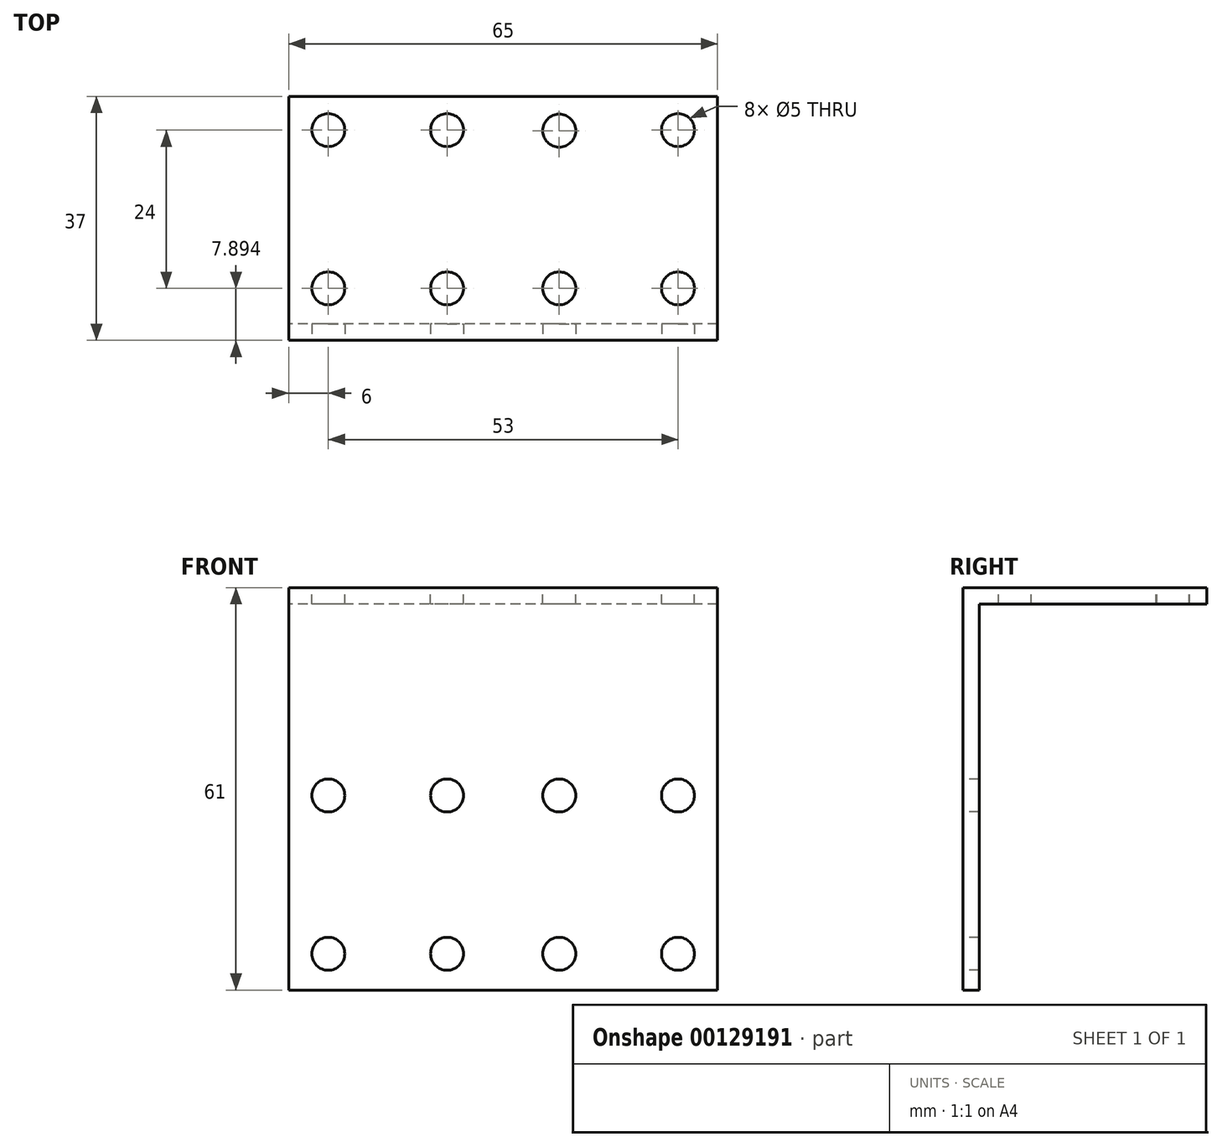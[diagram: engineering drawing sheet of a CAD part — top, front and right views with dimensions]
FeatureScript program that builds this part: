
annotation { "Feature Type Name" : "Feature", "Feature Type Description" : "" }
export const myFeature = defineFeature(function(context is Context, id is Id, definition is map)
    precondition{}
    {
        {
            var Q0;
            Q0=qCreatedBy(makeId("Right.planeOp"),FACE);
            var sketch = newSketch(context, id + "F0", { "sketchPlane" : qUnion([Q0])});
            skLineSegment(sketch, "E0.bottom", {"start": v(0, 0) * mm, "end": v(2.5, 0) * mm});
            skLineSegment(sketch, "E0.top", {"start": v(0, -58.5) * mm, "end": v(2.5, -58.5) * mm});
            skLineSegment(sketch, "E0.left", {"start": v(0, 0) * mm, "end": v(0, -58.5) * mm});
            skLineSegment(sketch, "E0.right", {"start": v(2.5, 0) * mm, "end": v(2.5, -58.5) * mm});
            skLineSegment(sketch, "E1.bottom", {"start": v(0, 0) * mm, "end": v(37, 0) * mm});
            skLineSegment(sketch, "E1.top", {"start": v(0, 2.5) * mm, "end": v(37, 2.5) * mm});
            skLineSegment(sketch, "E1.left", {"start": v(0, 0) * mm, "end": v(0, 2.5) * mm});
            skLineSegment(sketch, "E1.right", {"start": v(37, 0) * mm, "end": v(37, 2.5) * mm});
            skSolve(sketch);
        }
        {
            var Q0;
            Q0=makeQuery(id+"F0.imprint","IMPRINT",FACE,{"disambiguationData":[TD([[makeQuery(id+"F0.imprint","IMPRINT",EDGE,{"derivedFrom":sQuery(id+"F0.wireOp",EDGE,"E1.top")}),-1.0]])]});
            var Q1;
            Q1=makeQuery(id+"F0.imprint","IMPRINT",FACE,{"disambiguationData":[TD([[makeQuery(id+"F0.imprint","IMPRINT",EDGE,{"derivedFrom":sQuery(id+"F0.wireOp",EDGE,"E0.top")}),1.0]])]});
            extrude(context, id + "F1", {"entities" : qUnion([Q0, Q1]), "endBound" : BoundingType.SYMMETRIC, "depth" : 65 * mm});
        }
        {
            var Q0;
            Q0=qCreatedBy(makeId("Front.planeOp"),FACE);
            var sketch = newSketch(context, id + "F2", { "sketchPlane" : qUnion([Q0])});
            skLineSegment(sketch, "E2.bottom", {"start": v(-32.5, 2.5) * mm, "end": v(32.5, 2.5) * mm, "construction": true});
            skLineSegment(sketch, "E2.left", {"start": v(-32.5, 2.5) * mm, "end": v(-32.5, -32.5) * mm, "construction": true});
            skLineSegment(sketch, "E3", {"start": v(-34.69, -29) * mm, "end": v(41.82, -29) * mm, "construction": true});
            skCircle(sketch, "E4", {"center": v(-26.5, -29) * mm, "radius": 2.5 * mm});
            skCircle(sketch, "E5", {"center": v(-8.5, -29) * mm, "radius": 2.5 * mm});
            skCircle(sketch, "E6", {"center": v(8.5, -29) * mm, "radius": 2.5 * mm});
            skCircle(sketch, "E7", {"center": v(26.5, -29) * mm, "radius": 2.5 * mm});
            skLineSegment(sketch, "E8", {"start": v(-40, -53) * mm, "end": v(46.08, -53) * mm, "construction": true});
            skCircle(sketch, "E9", {"center": v(-26.5, -53) * mm, "radius": 2.5 * mm});
            skCircle(sketch, "E10", {"center": v(-8.5, -53) * mm, "radius": 2.5 * mm});
            skCircle(sketch, "E11", {"center": v(8.5, -53) * mm, "radius": 2.5 * mm});
            skCircle(sketch, "E12", {"center": v(26.5, -53) * mm, "radius": 2.5 * mm});
            skLineSegment(sketch, "E13", {"start": v(8.5, -15.9) * mm, "end": v(8.5, -70.5) * mm});
            skLineSegment(sketch, "E14", {"start": v(26.5, -15.26) * mm, "end": v(26.5, -64.56) * mm});
            skLineSegment(sketch, "E15", {"start": v(-8.5, -14.62) * mm, "end": v(-8.5, -68.69) * mm});
            skLineSegment(sketch, "E16", {"start": v(-26.5, -12.16) * mm, "end": v(-26.5, -65.46) * mm});
            skSolve(sketch);
        }
        {
            var Q0;
            Q0=makeQuery(id+"F2.imprint","IMPRINT",FACE,{"disambiguationData":[TD([[makeQuery(id+"F2.imprint","IMPRINT",EDGE,{"derivedFrom":sQuery(id+"F2.wireOp",EDGE,"E4")}),1.0]])]});
            var Q1;
            Q1=makeQuery(id+"F2.imprint","IMPRINT",FACE,{"disambiguationData":[TD([[makeQuery(id+"F2.imprint","IMPRINT",EDGE,{"derivedFrom":sQuery(id+"F2.wireOp",EDGE,"E5")}),1.0]])]});
            var Q2;
            Q2=makeQuery(id+"F2.imprint","IMPRINT",FACE,{"disambiguationData":[TD([[makeQuery(id+"F2.imprint","IMPRINT",EDGE,{"derivedFrom":sQuery(id+"F2.wireOp",EDGE,"E6")}),1.0]])]});
            var Q3;
            Q3=makeQuery(id+"F2.imprint","IMPRINT",FACE,{"disambiguationData":[TD([[makeQuery(id+"F2.imprint","IMPRINT",EDGE,{"derivedFrom":sQuery(id+"F2.wireOp",EDGE,"E7")}),1.0]])]});
            var Q4;
            Q4=makeQuery(id+"F2.imprint","IMPRINT",FACE,{"disambiguationData":[TD([[makeQuery(id+"F2.imprint","IMPRINT",EDGE,{"derivedFrom":sQuery(id+"F2.wireOp",EDGE,"E9")}),1.0]])]});
            var Q5;
            {var subQ0=sQuery(id+"F2.wireOp",EDGE,"E15");var subQ1=sQuery(id+"F2.wireOp",EDGE,"E10");var subQ2=makeQuery(id+"F2.imprint","INTERSECT",VERTEX,{"disambiguationData":[OD(0.0)],"derivedFrom":[subQ1,subQ0]});Q5=makeQuery(id+"F2.imprint","IMPRINT",FACE,{"disambiguationData":[TD([[makeQuery(id+"F2.imprint","IMPRINT",EDGE,{"disambiguationData":[TD([[subQ2,1.0]])],"derivedFrom":subQ1}),1.0]])]});}
            var Q6;
            {var subQ0=sQuery(id+"F2.wireOp",EDGE,"E15");var subQ1=sQuery(id+"F2.wireOp",EDGE,"E10");var subQ2=makeQuery(id+"F2.imprint","INTERSECT",VERTEX,{"disambiguationData":[OD(0.0)],"derivedFrom":[subQ1,subQ0]});Q6=makeQuery(id+"F2.imprint","IMPRINT",FACE,{"disambiguationData":[TD([[makeQuery(id+"F2.imprint","IMPRINT",EDGE,{"disambiguationData":[TD([[subQ2,-1.0]])],"derivedFrom":subQ1}),1.0]])]});}
            var Q7;
            {var subQ0=sQuery(id+"F2.wireOp",EDGE,"E13");var subQ1=sQuery(id+"F2.wireOp",EDGE,"E11");var subQ2=makeQuery(id+"F2.imprint","INTERSECT",VERTEX,{"disambiguationData":[OD(0.0)],"derivedFrom":[subQ1,subQ0]});Q7=makeQuery(id+"F2.imprint","IMPRINT",FACE,{"disambiguationData":[TD([[makeQuery(id+"F2.imprint","IMPRINT",EDGE,{"disambiguationData":[TD([[subQ2,1.0]])],"derivedFrom":subQ1}),1.0]])]});}
            var Q8;
            {var subQ0=sQuery(id+"F2.wireOp",EDGE,"E13");var subQ1=sQuery(id+"F2.wireOp",EDGE,"E11");var subQ2=makeQuery(id+"F2.imprint","INTERSECT",VERTEX,{"disambiguationData":[OD(0.0)],"derivedFrom":[subQ1,subQ0]});Q8=makeQuery(id+"F2.imprint","IMPRINT",FACE,{"disambiguationData":[TD([[makeQuery(id+"F2.imprint","IMPRINT",EDGE,{"disambiguationData":[TD([[subQ2,-1.0]])],"derivedFrom":subQ1}),1.0]])]});}
            var Q9;
            {var subQ0=sQuery(id+"F2.wireOp",EDGE,"E14");var subQ1=sQuery(id+"F2.wireOp",EDGE,"E12");var subQ2=makeQuery(id+"F2.imprint","INTERSECT",VERTEX,{"disambiguationData":[OD(0.0)],"derivedFrom":[subQ1,subQ0]});Q9=makeQuery(id+"F2.imprint","IMPRINT",FACE,{"disambiguationData":[TD([[makeQuery(id+"F2.imprint","IMPRINT",EDGE,{"disambiguationData":[TD([[subQ2,1.0]])],"derivedFrom":subQ1}),1.0]])]});}
            var Q10;
            {var subQ0=sQuery(id+"F2.wireOp",EDGE,"E14");var subQ1=sQuery(id+"F2.wireOp",EDGE,"E12");var subQ2=makeQuery(id+"F2.imprint","INTERSECT",VERTEX,{"disambiguationData":[OD(0.0)],"derivedFrom":[subQ1,subQ0]});Q10=makeQuery(id+"F2.imprint","IMPRINT",FACE,{"disambiguationData":[TD([[makeQuery(id+"F2.imprint","IMPRINT",EDGE,{"disambiguationData":[TD([[subQ2,-1.0]])],"derivedFrom":subQ1}),1.0]])]});}
            extrude(context, id + "F3", {"entities" : qUnion([Q0, Q1, Q2, Q3, Q4, Q5, Q6, Q7, Q8, Q9, Q10]), "operationType" : NewBodyOperationType.REMOVE, "endBound" : BoundingType.SYMMETRIC, "oppositeDirection" : true, "depth" : 10 * mm});
        }
        {
            var Q0;
            Q0=makeQuery(id+"F1.opExtrude","SWEPT_FACE",FACE,{"disambiguationData":[OSD([sQuery(id+"F0.wireOp",EDGE,"E1.top")])]});
            var sketch = newSketch(context, id + "F4", { "sketchPlane" : qUnion([Q0])});
            skLineSegment(sketch, "E17", {"start": v(-26.5, 45.64) * mm, "end": v(-26.5, -8.44) * mm, "construction": true});
            skLineSegment(sketch, "E18", {"start": v(-42.57, 7.9) * mm, "end": v(45.18, 7.9) * mm, "construction": true});
            skCircle(sketch, "E19", {"center": v(-26.5, 7.9) * mm, "radius": 2.5 * mm});
            skCircle(sketch, "E20", {"center": v(-8.5, 7.9) * mm, "radius": 2.5 * mm});
            skCircle(sketch, "E21", {"center": v(8.5, 7.9) * mm, "radius": 2.5 * mm});
            skCircle(sketch, "E22", {"center": v(26.5, 7.9) * mm, "radius": 2.5 * mm});
            skLineSegment(sketch, "E23", {"start": v(-43.35, 31.9) * mm, "end": v(45.05, 31.9) * mm, "construction": true});
            skCircle(sketch, "E24", {"center": v(-26.5, 31.9) * mm, "radius": 2.5 * mm});
            skCircle(sketch, "E25", {"center": v(-8.5, 31.9) * mm, "radius": 2.5 * mm});
            skCircle(sketch, "E26", {"center": v(8.5, 31.8) * mm, "radius": 2.5 * mm});
            skCircle(sketch, "E27", {"center": v(26.5, 31.9) * mm, "radius": 2.5 * mm});
            skSolve(sketch);
        }
        {
            var Q0;
            Q0=makeQuery(id+"F4.imprint","IMPRINT",FACE,{"disambiguationData":[TD([[makeQuery(id+"F4.imprint","IMPRINT",EDGE,{"derivedFrom":sQuery(id+"F4.wireOp",EDGE,"E19")}),1.0]])]});
            var Q1;
            Q1=makeQuery(id+"F4.imprint","IMPRINT",FACE,{"disambiguationData":[TD([[makeQuery(id+"F4.imprint","IMPRINT",EDGE,{"derivedFrom":sQuery(id+"F4.wireOp",EDGE,"E24")}),1.0]])]});
            var Q2;
            Q2=makeQuery(id+"F4.imprint","IMPRINT",FACE,{"disambiguationData":[TD([[makeQuery(id+"F4.imprint","IMPRINT",EDGE,{"derivedFrom":sQuery(id+"F4.wireOp",EDGE,"E25")}),1.0]])]});
            var Q3;
            Q3=makeQuery(id+"F4.imprint","IMPRINT",FACE,{"disambiguationData":[TD([[makeQuery(id+"F4.imprint","IMPRINT",EDGE,{"derivedFrom":sQuery(id+"F4.wireOp",EDGE,"E20")}),1.0]])]});
            var Q4;
            Q4=makeQuery(id+"F4.imprint","IMPRINT",FACE,{"disambiguationData":[TD([[makeQuery(id+"F4.imprint","IMPRINT",EDGE,{"derivedFrom":sQuery(id+"F4.wireOp",EDGE,"E21")}),1.0]])]});
            var Q5;
            Q5=makeQuery(id+"F4.imprint","IMPRINT",FACE,{"disambiguationData":[TD([[makeQuery(id+"F4.imprint","IMPRINT",EDGE,{"derivedFrom":sQuery(id+"F4.wireOp",EDGE,"E26")}),1.0]])]});
            var Q6;
            Q6=makeQuery(id+"F4.imprint","IMPRINT",FACE,{"disambiguationData":[TD([[makeQuery(id+"F4.imprint","IMPRINT",EDGE,{"derivedFrom":sQuery(id+"F4.wireOp",EDGE,"E27")}),1.0]])]});
            var Q7;
            Q7=makeQuery(id+"F4.imprint","IMPRINT",FACE,{"disambiguationData":[TD([[makeQuery(id+"F4.imprint","IMPRINT",EDGE,{"derivedFrom":sQuery(id+"F4.wireOp",EDGE,"E22")}),1.0]])]});
            extrude(context, id + "F5", {"entities" : qUnion([Q0, Q1, Q2, Q3, Q4, Q5, Q6, Q7]), "operationType" : NewBodyOperationType.REMOVE, "endBound" : BoundingType.SYMMETRIC, "oppositeDirection" : true, "depth" : 10 * mm});
        }
    });
